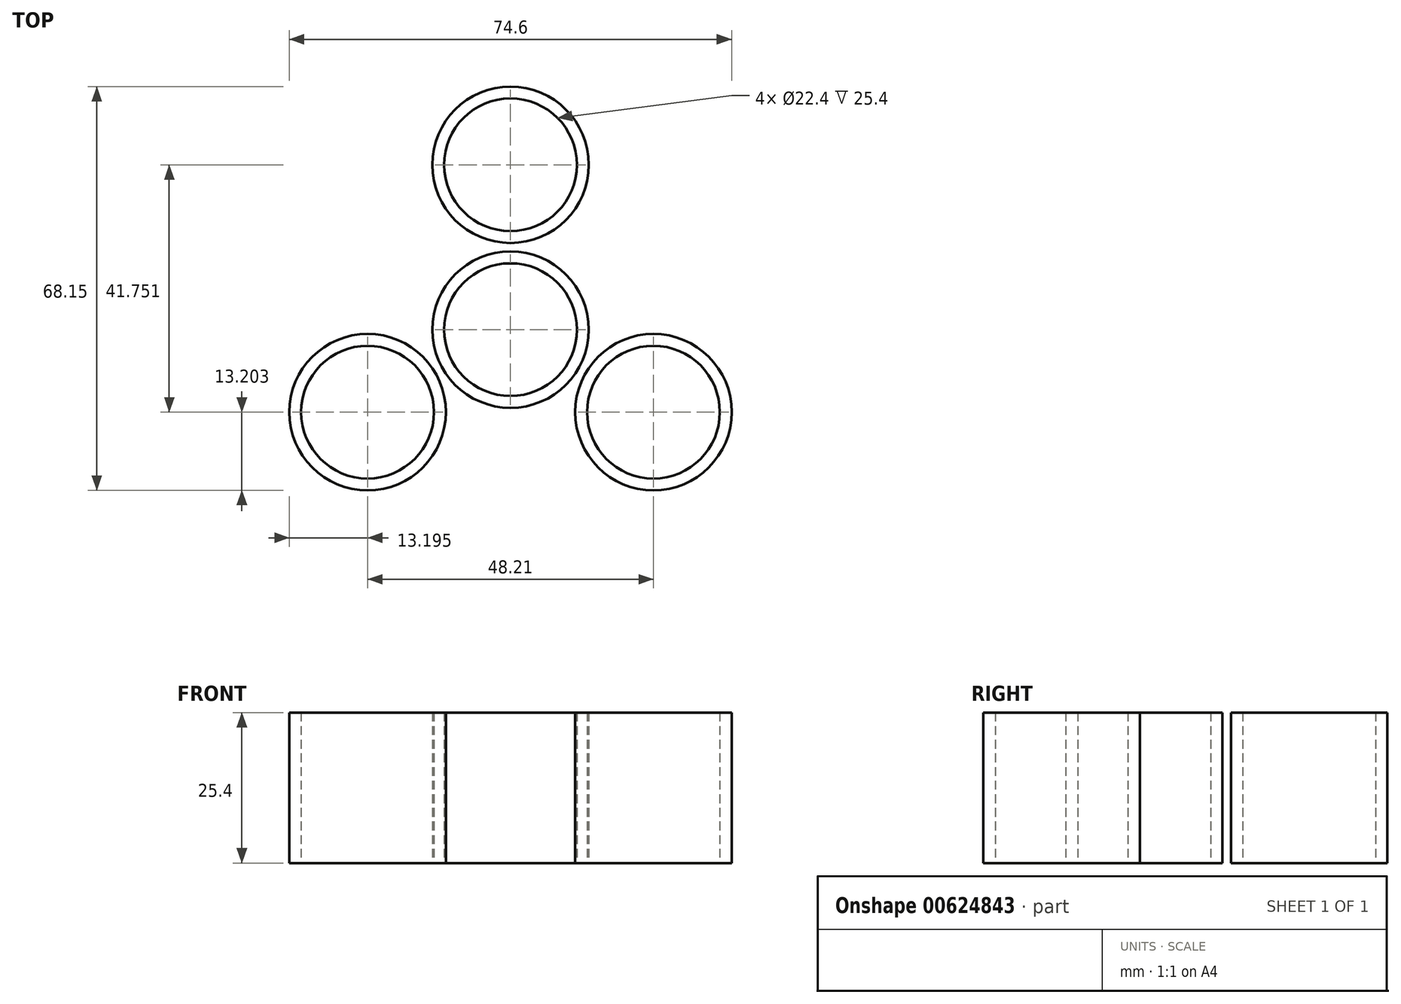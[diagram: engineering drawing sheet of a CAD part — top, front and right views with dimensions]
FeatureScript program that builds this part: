
annotation { "Feature Type Name" : "Feature", "Feature Type Description" : "" }
export const myFeature = defineFeature(function(context is Context, id is Id, definition is map)
    precondition{}
    {
        {
            var Q0;
            Q0=qCreatedBy(makeId("Top.planeOp"),FACE);
            var sketch = newSketch(context, id + "F0", { "sketchPlane" : qUnion([Q0])});
            skCircle(sketch, "E0", {"center": v(0, 0) * mm, "radius": 11.2 * mm});
            skCircle(sketch, "E1", {"center": v(0, 0) * mm, "radius": 13.2 * mm});
            skCircle(sketch, "E2", {"center": v(0, 27.83) * mm, "radius": 11.2 * mm});
            skCircle(sketch, "E3", {"center": v(0, 27.83) * mm, "radius": 13.2 * mm});
            skCircle(sketch, "E4.1.0", {"center": v(-24.1, -13.92) * mm, "radius": 13.2 * mm});
            skCircle(sketch, "E4.1.1", {"center": v(-24.1, -13.92) * mm, "radius": 11.2 * mm});
            skCircle(sketch, "E4.2.0", {"center": v(24.1, -13.92) * mm, "radius": 13.2 * mm});
            skCircle(sketch, "E4.2.1", {"center": v(24.1, -13.92) * mm, "radius": 11.2 * mm});
            skLineSegment(sketch, "E5", {"start": v(-24.1, -13.92) * mm, "end": v(0, 0) * mm, "construction": true});
            skLineSegment(sketch, "E6", {"start": v(-24.1, -13.92) * mm, "end": v(55.35, 31.96) * mm, "construction": true});
            skLineSegment(sketch, "E7", {"start": v(0, 27.83) * mm, "end": v(24.1, -13.92) * mm, "construction": true});
            skLineSegment(sketch, "E8.1.0", {"start": v(-24.1, -13.92) * mm, "end": v(0, 27.83) * mm, "construction": true});
            skLineSegment(sketch, "E8.2.0", {"start": v(24.1, -13.92) * mm, "end": v(-24.1, -13.92) * mm, "construction": true});
            skSolve(sketch);
        }
        {
            var Q0;
            Q0 = qSketchRegion(id + "F0", true);
            extrude(context, id + "F1", {"entities" : qUnion([Q0]), "depth" : 25.4 * mm, "offsetDistance" : 25.4 * mm});
        }
    });
